# Revit family: HA07510000
name_source: partatom
category: Apparecchi idraulici
units: mm (PartAtom-declared; Revit-internal decimal feet)

## family parameters
Basato su piano di lavoro = No
Condiviso = No
Numero OmniClass = 23.45.00.00
Punto di calcolo locali = No
Quota connettore circolare = Usa diametro
Sempre verticale = Sì
Taglio con vuoti quando caricato = No
Tipo di parte = Normale
Titolo OmniClass = Sanitary, Laundry, and Cleaning Equipment

## types (1)
- HA07510000
    Commenti sul tipo = Utilizzato nei più svariati settori dell'impiantistica: reti di distribuzione acqua potabile, impianti di riscaldamento, condizionamento, igienico-sanitari e in generale con ogni fluido non corrosivo
    Descrizione = Realizzato in ottemperanza ai requisiti gestionali della norma EN ISO 9001.
Utilizzato per la regolazione della temperatura degli ambienti e comandare apparecchi degli impianti di riscaldamento e condizionamento.
    Materiale = Prodotto in lega di ottone conforme alla norma EN 12165-CW617N-DW
    Modello = Cim 751
    Produttore = CIMBERIO SPA
    Prospetto di default = 0 mm  [stored 0 ft]
    URL = https://web.cimberio.com

note: [stored X ft] marks values corroborated as IEEE doubles in the binary element streams (Revit-internal decimal feet)
